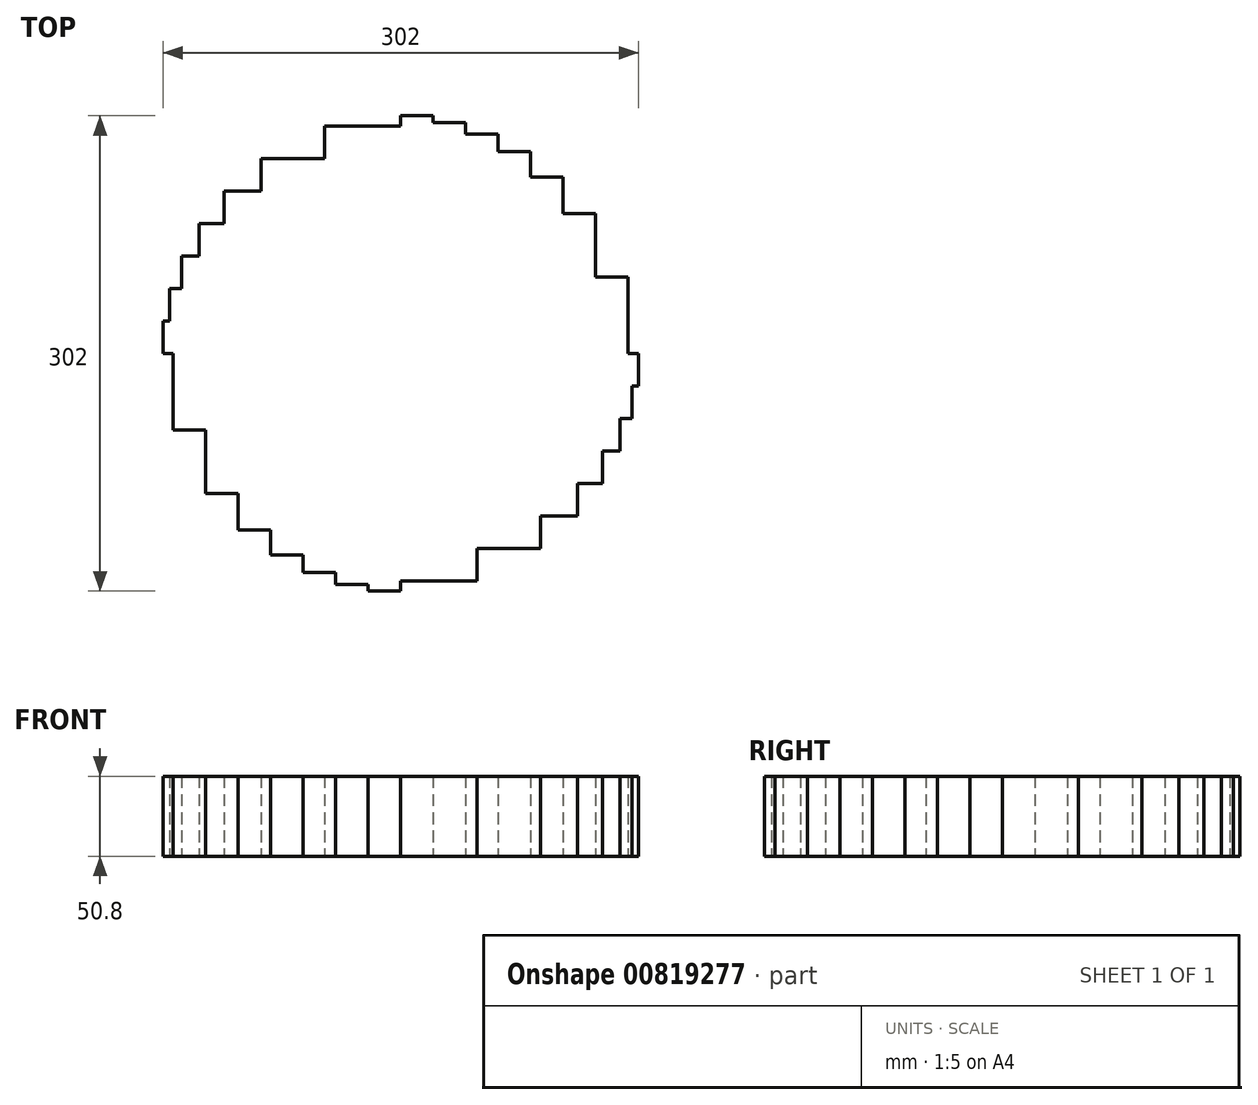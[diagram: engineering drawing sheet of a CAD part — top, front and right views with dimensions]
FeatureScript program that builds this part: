
annotation { "Feature Type Name" : "Feature", "Feature Type Description" : "" }
export const myFeature = defineFeature(function(context is Context, id is Id, definition is map)
    precondition{}
    {
        {
            var Q0;
            Q0=qCreatedBy(makeId("Top.planeOp"),FACE);
            var sketch = newSketch(context, id + "F0", { "sketchPlane" : qUnion([Q0])});
            skCircle(sketch, "E0", {"center": v(0, 0) * mm, "radius": 152.4 * mm, "construction": true});
            skLineSegment(sketch, "E1", {"start": v(0, 187.55) * mm, "end": v(0, -210.06) * mm, "construction": true});
            skLineSegment(sketch, "E2", {"start": v(-253.27, 0) * mm, "end": v(308.24, 0) * mm, "construction": true});
            skLineSegment(sketch, "E3.bottom", {"start": v(0, 0) * mm, "end": v(-20.64, 0) * mm});
            skLineSegment(sketch, "E3.top", {"start": v(0, -151) * mm, "end": v(-20.64, -151) * mm});
            skLineSegment(sketch, "E3.left", {"start": v(0, 0) * mm, "end": v(0, -151) * mm});
            skLineSegment(sketch, "E3.right", {"start": v(-20.64, 0) * mm, "end": v(-20.64, -151) * mm});
            skLineSegment(sketch, "E4.bottom", {"start": v(-20.64, 0) * mm, "end": v(-41.28, 0) * mm});
            skLineSegment(sketch, "E4.top", {"start": v(-20.64, -146.7) * mm, "end": v(-41.27, -146.7) * mm});
            skLineSegment(sketch, "E4.left", {"start": v(-20.64, 0) * mm, "end": v(-20.64, -146.7) * mm});
            skLineSegment(sketch, "E4.right", {"start": v(-41.28, 0) * mm, "end": v(-41.27, -146.7) * mm});
            skLineSegment(sketch, "E5.bottom", {"start": v(-41.28, 0) * mm, "end": v(-61.91, 0) * mm});
            skLineSegment(sketch, "E5.top", {"start": v(-41.28, -139.26) * mm, "end": v(-61.91, -139.26) * mm});
            skLineSegment(sketch, "E5.left", {"start": v(-41.28, 0) * mm, "end": v(-41.28, -139.26) * mm});
            skLineSegment(sketch, "E5.right", {"start": v(-61.91, 0) * mm, "end": v(-61.91, -139.26) * mm});
            skLineSegment(sketch, "E6.bottom", {"start": v(-61.91, 0) * mm, "end": v(-82.55, 0) * mm});
            skLineSegment(sketch, "E6.top", {"start": v(-61.91, -128.1) * mm, "end": v(-82.55, -128.1) * mm});
            skLineSegment(sketch, "E6.left", {"start": v(-61.91, 0) * mm, "end": v(-61.91, -128.1) * mm});
            skLineSegment(sketch, "E6.right", {"start": v(-82.55, 0) * mm, "end": v(-82.55, -128.1) * mm});
            skLineSegment(sketch, "E7.bottom", {"start": v(-82.55, 0) * mm, "end": v(-103.19, 0) * mm});
            skLineSegment(sketch, "E7.top", {"start": v(-82.55, -112.15) * mm, "end": v(-103.19, -112.15) * mm});
            skLineSegment(sketch, "E7.left", {"start": v(-82.55, 0) * mm, "end": v(-82.55, -112.15) * mm});
            skLineSegment(sketch, "E7.right", {"start": v(-103.19, 0) * mm, "end": v(-103.19, -112.15) * mm});
            skLineSegment(sketch, "E8.bottom", {"start": v(-103.19, 0) * mm, "end": v(-123.83, 0) * mm});
            skLineSegment(sketch, "E8.top", {"start": v(-103.19, -88.84) * mm, "end": v(-123.83, -88.84) * mm});
            skLineSegment(sketch, "E8.left", {"start": v(-103.19, 0) * mm, "end": v(-103.19, -88.84) * mm});
            skLineSegment(sketch, "E8.right", {"start": v(-123.83, 0) * mm, "end": v(-123.83, -88.84) * mm});
            skLineSegment(sketch, "E9.bottom", {"start": v(-123.83, 0) * mm, "end": v(-144.46, 0) * mm});
            skLineSegment(sketch, "E9.top", {"start": v(-123.83, -48.54) * mm, "end": v(-144.46, -48.54) * mm});
            skLineSegment(sketch, "E9.left", {"start": v(-123.83, 0) * mm, "end": v(-123.83, -48.54) * mm});
            skLineSegment(sketch, "E9.right", {"start": v(-144.46, 0) * mm, "end": v(-144.46, -48.54) * mm});
            skLineSegment(sketch, "E10.1.0", {"start": v(0, -20.64) * mm, "end": v(0, -41.28) * mm});
            skLineSegment(sketch, "E10.1.1", {"start": v(146.7, -20.64) * mm, "end": v(146.7, -41.28) * mm});
            skLineSegment(sketch, "E10.1.2", {"start": v(0, -20.64) * mm, "end": v(146.7, -20.64) * mm});
            skLineSegment(sketch, "E10.1.3", {"start": v(0, -41.28) * mm, "end": v(146.7, -41.28) * mm});
            skLineSegment(sketch, "E10.1.4", {"start": v(0, -41.28) * mm, "end": v(0, -61.91) * mm});
            skLineSegment(sketch, "E10.1.5", {"start": v(139.26, -41.28) * mm, "end": v(139.26, -61.91) * mm});
            skLineSegment(sketch, "E10.1.6", {"start": v(0, 0) * mm, "end": v(151, 0) * mm});
            skLineSegment(sketch, "E10.1.7", {"start": v(151, 0) * mm, "end": v(151, -20.64) * mm});
            skLineSegment(sketch, "E10.1.8", {"start": v(0, -123.83) * mm, "end": v(0, -144.46) * mm});
            skLineSegment(sketch, "E10.1.9", {"start": v(0, -103.19) * mm, "end": v(0, -123.83) * mm});
            skLineSegment(sketch, "E10.1.10", {"start": v(0, -103.19) * mm, "end": v(112.15, -103.19) * mm});
            skLineSegment(sketch, "E10.1.11", {"start": v(0, 0) * mm, "end": v(0, -20.64) * mm});
            skLineSegment(sketch, "E10.1.12", {"start": v(0, -61.91) * mm, "end": v(0, -82.55) * mm});
            skLineSegment(sketch, "E10.1.13", {"start": v(0, -61.91) * mm, "end": v(139.26, -61.91) * mm});
            skLineSegment(sketch, "E10.1.14", {"start": v(112.15, -82.55) * mm, "end": v(112.15, -103.19) * mm});
            skLineSegment(sketch, "E10.1.15", {"start": v(0, -82.55) * mm, "end": v(128.1, -82.55) * mm});
            skLineSegment(sketch, "E10.1.16", {"start": v(0, -123.83) * mm, "end": v(48.54, -123.83) * mm});
            skLineSegment(sketch, "E10.1.17", {"start": v(128.1, -61.91) * mm, "end": v(128.1, -82.55) * mm});
            skLineSegment(sketch, "E10.1.18", {"start": v(0, -82.55) * mm, "end": v(0, -103.19) * mm});
            skLineSegment(sketch, "E10.1.19", {"start": v(0, -144.46) * mm, "end": v(48.54, -144.46) * mm});
            skLineSegment(sketch, "E10.1.20", {"start": v(88.84, -103.19) * mm, "end": v(88.84, -123.83) * mm});
            skLineSegment(sketch, "E10.1.21", {"start": v(0, -123.83) * mm, "end": v(88.84, -123.83) * mm});
            skLineSegment(sketch, "E10.1.22", {"start": v(48.54, -123.83) * mm, "end": v(48.54, -144.46) * mm});
            skLineSegment(sketch, "E10.1.23", {"start": v(0, -20.64) * mm, "end": v(151, -20.64) * mm});
            skLineSegment(sketch, "E10.1.24", {"start": v(0, -103.19) * mm, "end": v(88.84, -103.19) * mm});
            skLineSegment(sketch, "E10.1.25", {"start": v(0, -41.28) * mm, "end": v(139.26, -41.28) * mm});
            skLineSegment(sketch, "E10.1.26", {"start": v(0, -61.91) * mm, "end": v(128.1, -61.91) * mm});
            skLineSegment(sketch, "E10.1.27", {"start": v(0, -82.55) * mm, "end": v(112.15, -82.55) * mm});
            skLineSegment(sketch, "E10.2.0", {"start": v(20.64, 0) * mm, "end": v(41.28, 0) * mm});
            skLineSegment(sketch, "E10.2.1", {"start": v(20.64, 146.7) * mm, "end": v(41.28, 146.7) * mm});
            skLineSegment(sketch, "E10.2.2", {"start": v(20.64, 0) * mm, "end": v(20.64, 146.7) * mm});
            skLineSegment(sketch, "E10.2.3", {"start": v(41.28, 0) * mm, "end": v(41.28, 146.7) * mm});
            skLineSegment(sketch, "E10.2.4", {"start": v(41.28, 0) * mm, "end": v(61.91, 0) * mm});
            skLineSegment(sketch, "E10.2.5", {"start": v(41.28, 139.26) * mm, "end": v(61.91, 139.26) * mm});
            skLineSegment(sketch, "E10.2.6", {"start": v(0, 0) * mm, "end": v(0, 151) * mm});
            skLineSegment(sketch, "E10.2.7", {"start": v(0, 151) * mm, "end": v(20.64, 151) * mm});
            skLineSegment(sketch, "E10.2.8", {"start": v(123.83, 0) * mm, "end": v(144.46, 0) * mm});
            skLineSegment(sketch, "E10.2.9", {"start": v(103.19, 0) * mm, "end": v(123.83, 0) * mm});
            skLineSegment(sketch, "E10.2.10", {"start": v(103.19, 0) * mm, "end": v(103.19, 112.15) * mm});
            skLineSegment(sketch, "E10.2.11", {"start": v(0, 0) * mm, "end": v(20.64, 0) * mm});
            skLineSegment(sketch, "E10.2.12", {"start": v(61.91, 0) * mm, "end": v(82.55, 0) * mm});
            skLineSegment(sketch, "E10.2.13", {"start": v(61.91, 0) * mm, "end": v(61.91, 139.26) * mm});
            skLineSegment(sketch, "E10.2.14", {"start": v(82.55, 112.15) * mm, "end": v(103.19, 112.15) * mm});
            skLineSegment(sketch, "E10.2.15", {"start": v(82.55, 0) * mm, "end": v(82.55, 128.1) * mm});
            skLineSegment(sketch, "E10.2.16", {"start": v(123.83, 0) * mm, "end": v(123.83, 48.54) * mm});
            skLineSegment(sketch, "E10.2.17", {"start": v(61.91, 128.1) * mm, "end": v(82.55, 128.1) * mm});
            skLineSegment(sketch, "E10.2.18", {"start": v(82.55, 0) * mm, "end": v(103.19, 0) * mm});
            skLineSegment(sketch, "E10.2.19", {"start": v(144.46, 0) * mm, "end": v(144.46, 48.54) * mm});
            skLineSegment(sketch, "E10.2.20", {"start": v(103.19, 88.84) * mm, "end": v(123.83, 88.84) * mm});
            skLineSegment(sketch, "E10.2.21", {"start": v(123.83, 0) * mm, "end": v(123.83, 88.84) * mm});
            skLineSegment(sketch, "E10.2.22", {"start": v(123.83, 48.54) * mm, "end": v(144.46, 48.54) * mm});
            skLineSegment(sketch, "E10.2.23", {"start": v(20.64, 0) * mm, "end": v(20.64, 151) * mm});
            skLineSegment(sketch, "E10.2.24", {"start": v(103.19, 0) * mm, "end": v(103.19, 88.84) * mm});
            skLineSegment(sketch, "E10.2.25", {"start": v(41.28, 0) * mm, "end": v(41.28, 139.26) * mm});
            skLineSegment(sketch, "E10.2.26", {"start": v(61.91, 0) * mm, "end": v(61.91, 128.1) * mm});
            skLineSegment(sketch, "E10.2.27", {"start": v(82.55, 0) * mm, "end": v(82.55, 112.15) * mm});
            skLineSegment(sketch, "E10.3.0", {"start": v(0, 20.64) * mm, "end": v(0, 41.28) * mm});
            skLineSegment(sketch, "E10.3.1", {"start": v(-146.7, 20.64) * mm, "end": v(-146.7, 41.28) * mm});
            skLineSegment(sketch, "E10.3.2", {"start": v(0, 20.64) * mm, "end": v(-146.7, 20.64) * mm});
            skLineSegment(sketch, "E10.3.3", {"start": v(0, 41.28) * mm, "end": v(-146.7, 41.28) * mm});
            skLineSegment(sketch, "E10.3.4", {"start": v(0, 41.28) * mm, "end": v(0, 61.91) * mm});
            skLineSegment(sketch, "E10.3.5", {"start": v(-139.26, 41.28) * mm, "end": v(-139.26, 61.91) * mm});
            skLineSegment(sketch, "E10.3.6", {"start": v(0, 0) * mm, "end": v(-151, 0) * mm});
            skLineSegment(sketch, "E10.3.7", {"start": v(-151, 0) * mm, "end": v(-151, 20.64) * mm});
            skLineSegment(sketch, "E10.3.8", {"start": v(0, 123.83) * mm, "end": v(0, 144.46) * mm});
            skLineSegment(sketch, "E10.3.9", {"start": v(0, 103.19) * mm, "end": v(0, 123.83) * mm});
            skLineSegment(sketch, "E10.3.10", {"start": v(0, 103.19) * mm, "end": v(-112.15, 103.19) * mm});
            skLineSegment(sketch, "E10.3.11", {"start": v(0, 0) * mm, "end": v(0, 20.64) * mm});
            skLineSegment(sketch, "E10.3.12", {"start": v(0, 61.91) * mm, "end": v(0, 82.55) * mm});
            skLineSegment(sketch, "E10.3.13", {"start": v(0, 61.91) * mm, "end": v(-139.26, 61.91) * mm});
            skLineSegment(sketch, "E10.3.14", {"start": v(-112.15, 82.55) * mm, "end": v(-112.15, 103.19) * mm});
            skLineSegment(sketch, "E10.3.15", {"start": v(0, 82.55) * mm, "end": v(-128.1, 82.55) * mm});
            skLineSegment(sketch, "E10.3.16", {"start": v(0, 123.83) * mm, "end": v(-48.54, 123.83) * mm});
            skLineSegment(sketch, "E10.3.17", {"start": v(-128.1, 61.91) * mm, "end": v(-128.1, 82.55) * mm});
            skLineSegment(sketch, "E10.3.18", {"start": v(0, 82.55) * mm, "end": v(0, 103.19) * mm});
            skLineSegment(sketch, "E10.3.19", {"start": v(0, 144.46) * mm, "end": v(-48.54, 144.46) * mm});
            skLineSegment(sketch, "E10.3.20", {"start": v(-88.84, 103.19) * mm, "end": v(-88.84, 123.83) * mm});
            skLineSegment(sketch, "E10.3.21", {"start": v(0, 123.83) * mm, "end": v(-88.84, 123.83) * mm});
            skLineSegment(sketch, "E10.3.22", {"start": v(-48.54, 123.83) * mm, "end": v(-48.54, 144.46) * mm});
            skLineSegment(sketch, "E10.3.23", {"start": v(0, 20.64) * mm, "end": v(-151, 20.64) * mm});
            skLineSegment(sketch, "E10.3.24", {"start": v(0, 103.19) * mm, "end": v(-88.84, 103.19) * mm});
            skLineSegment(sketch, "E10.3.25", {"start": v(0, 41.28) * mm, "end": v(-139.26, 41.28) * mm});
            skLineSegment(sketch, "E10.3.26", {"start": v(0, 61.91) * mm, "end": v(-128.1, 61.91) * mm});
            skLineSegment(sketch, "E10.3.27", {"start": v(0, 82.55) * mm, "end": v(-112.15, 82.55) * mm});
            skSolve(sketch);
        }
        {
            var Q0;
            Q0 = qSketchRegion(id + "F0", true);
            extrude(context, id + "F1", {"entities" : qUnion([Q0]), "depth" : 50.8 * mm, "offsetDistance" : 25.4 * mm});
        }
    });
